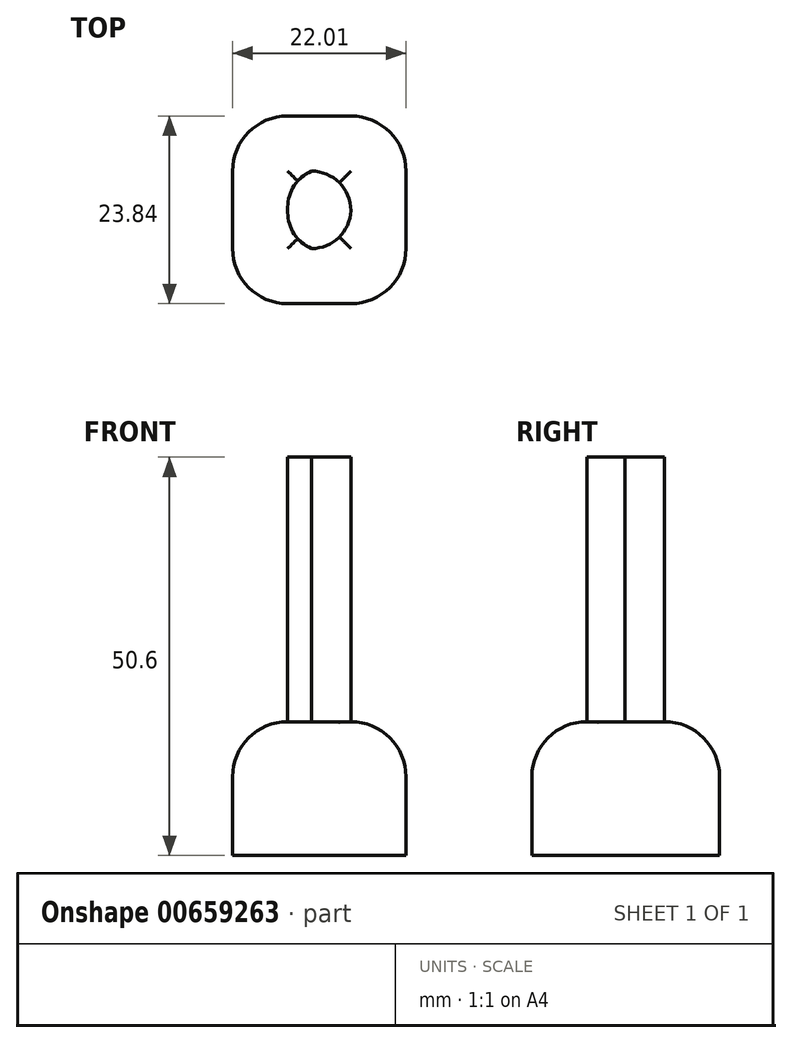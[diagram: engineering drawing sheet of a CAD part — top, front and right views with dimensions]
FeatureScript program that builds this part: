
annotation { "Feature Type Name" : "Feature", "Feature Type Description" : "" }
export const myFeature = defineFeature(function(context is Context, id is Id, definition is map)
    precondition{}
    {
        {
            var Q0;
            Q0=qCreatedBy(makeId("Top.planeOp"),FACE);
            var sketch = newSketch(context, id + "F0", { "sketchPlane" : qUnion([Q0])});
            skLineSegment(sketch, "E0.bottom", {"start": v(-41.92, -36.53) * mm, "end": v(-63.93, -36.53) * mm});
            skLineSegment(sketch, "E0.top", {"start": v(-41.92, -60.37) * mm, "end": v(-63.93, -60.37) * mm});
            skLineSegment(sketch, "E0.left", {"start": v(-41.92, -36.53) * mm, "end": v(-41.92, -60.37) * mm});
            skLineSegment(sketch, "E0.right", {"start": v(-63.93, -36.53) * mm, "end": v(-63.93, -60.37) * mm});
            skPoint(sketch, "E0.middle", {"position": v(-52.93, -48.45) * mm});
            skSolve(sketch);
        }
        {
            var Q0;
            Q0 = qSketchRegion(id + "F0", true);
            extrude(context, id + "F1", {"entities" : qUnion([Q0]), "depth" : 17 * mm, "offsetDistance" : 25 * mm});
        }
        {
            var Q0;
            Q0=makeQuery(id+"F1.opExtrude","CAP_EDGE",EDGE,{"disambiguationData":[OSD([sQuery(id+"F0.wireOp",EDGE,"E0.top")])],"isStart":false});
            fillet(context, id + "F2", {"entities" : qUnion([Q0]), "radius" : 7 * mm, "tangentPropagation" : true, "allowEdgeOverflow" : false});
        }
        {
            var Q0;
            Q0=makeQuery(id+"F1.opExtrude","CAP_EDGE",EDGE,{"disambiguationData":[OSD([sQuery(id+"F0.wireOp",EDGE,"E0.bottom")])],"isStart":false});
            var Q1;
            Q1=makeQuery(id+"F1.opExtrude","CAP_EDGE",EDGE,{"disambiguationData":[OSD([sQuery(id+"F0.wireOp",EDGE,"E0.left")])],"isStart":false});
            var Q2;
            Q2=makeQuery(id+"F1.opExtrude","CAP_EDGE",EDGE,{"disambiguationData":[OSD([sQuery(id+"F0.wireOp",EDGE,"E0.right")])],"isStart":false});
            fillet(context, id + "F3", {"entities" : qUnion([Q0, Q1, Q2]), "radius" : 7 * mm, "tangentPropagation" : true, "allowEdgeOverflow" : false});
        }
        {
            var Q0;
            Q0=makeQuery(id+"F1.opExtrude","SWEPT_EDGE",EDGE,{"disambiguationData":[OSD([sQuery(id+"F0.wireOp",EDGE,"E0.bottom"),sQuery(id+"F0.wireOp",EDGE,"E0.right")])]});
            fillet(context, id + "F4", {"entities" : qUnion([Q0]), "radius" : 7 * mm, "tangentPropagation" : true, "allowEdgeOverflow" : false});
        }
        {
            var Q0;
            Q0=makeQuery(id+"F1.opExtrude","SWEPT_EDGE",EDGE,{"disambiguationData":[OSD([sQuery(id+"F0.wireOp",EDGE,"E0.bottom"),sQuery(id+"F0.wireOp",EDGE,"E0.left")])]});
            fillet(context, id + "F5", {"entities" : qUnion([Q0]), "radius" : 7 * mm, "tangentPropagation" : true, "allowEdgeOverflow" : false});
        }
        {
            var Q0;
            Q0=makeQuery(id+"F1.opExtrude","CAP_FACE",FACE,{"disambiguationData":[OSD([sQuery(id+"F0.wireOp",EDGE,"E0.bottom"),sQuery(id+"F0.wireOp",EDGE,"E0.top"),sQuery(id+"F0.wireOp",EDGE,"E0.left"),sQuery(id+"F0.wireOp",EDGE,"E0.right")])],"isStart":false});
            extrude(context, id + "F6", {"entities" : qUnion([Q0]), "operationType" : NewBodyOperationType.ADD, "depth" : 33.6 * mm, "offsetDistance" : 25 * mm});
        }
        {
            var Q0;
            {var subQ0=sQuery(id+"F0.wireOp",EDGE,"E0.bottom");var subQ1=sQuery(id+"F0.wireOp",EDGE,"E0.right");var subQ2=sQuery(id+"F0.wireOp",EDGE,"E0.left");var subQ3=sQuery(id+"F0.wireOp",EDGE,"E0.top");Q0=makeQuery(id+"F6.opExtrude","SWEPT_EDGE",EDGE,{"disambiguationData":[OSD([subQ0,subQ3,subQ2,subQ1]),TDD([makeQuery(id+"F5.opFillet","BLEND_VERTEX",VERTEX,{"blendedFrom":[makeQuery(id+"F3.opFillet","BLEND_EDGE",EDGE,{"blendedFrom":[makeQuery(id+"F1.opExtrude","CAP_EDGE",EDGE,{"disambiguationData":[OSD([subQ0])],"isStart":false}),makeQuery(id+"F1.opExtrude","CAP_EDGE",EDGE,{"disambiguationData":[OSD([subQ2])],"isStart":false})],"blendedInto":[]}),makeQuery(id+"F3.opFillet","BLEND_FACE",FACE,{"disambiguationData":[OSD([subQ2])]}),makeQuery(id+"F1.opExtrude","CAP_FACE",FACE,{"disambiguationData":[OSD([subQ0,subQ3,subQ2,subQ1])],"isStart":false}),makeQuery(id+"F3.opFillet","BLEND_FACE",FACE,{"disambiguationData":[OSD([subQ0])]})],"blendedInto":[makeQuery(id+"F3.opFillet","BLEND_FACE",FACE,{"disambiguationData":[OSD([subQ2])]}),makeQuery(id+"F1.opExtrude","CAP_FACE",FACE,{"disambiguationData":[OSD([subQ0,subQ3,subQ2,subQ1])],"isStart":false}),makeQuery(id+"F3.opFillet","BLEND_FACE",FACE,{"disambiguationData":[OSD([subQ0])]})]})])]});}
            fillet(context, id + "F7", {"entities" : qUnion([Q0]), "radius" : 5 * mm, "tangentPropagation" : true, "allowEdgeOverflow" : false});
        }
        {
            var Q0;
            {var subQ0=sQuery(id+"F0.wireOp",EDGE,"E0.right");var subQ1=sQuery(id+"F0.wireOp",EDGE,"E0.left");var subQ2=sQuery(id+"F0.wireOp",EDGE,"E0.top");var subQ3=sQuery(id+"F0.wireOp",EDGE,"E0.bottom");Q0=makeQuery(id+"F6.opExtrude","SWEPT_EDGE",EDGE,{"disambiguationData":[OSD([subQ3,subQ2,subQ1,subQ0]),TDD([makeQuery(id+"F4.opFillet","BLEND_VERTEX",VERTEX,{"blendedFrom":[makeQuery(id+"F3.opFillet","BLEND_EDGE",EDGE,{"blendedFrom":[makeQuery(id+"F1.opExtrude","CAP_EDGE",EDGE,{"disambiguationData":[OSD([subQ3])],"isStart":false}),makeQuery(id+"F1.opExtrude","CAP_EDGE",EDGE,{"disambiguationData":[OSD([subQ0])],"isStart":false})],"blendedInto":[]}),makeQuery(id+"F3.opFillet","BLEND_FACE",FACE,{"disambiguationData":[OSD([subQ3])]}),makeQuery(id+"F3.opFillet","BLEND_FACE",FACE,{"disambiguationData":[OSD([subQ0])]}),makeQuery(id+"F1.opExtrude","CAP_FACE",FACE,{"disambiguationData":[OSD([subQ3,subQ2,subQ1,subQ0])],"isStart":false})],"blendedInto":[makeQuery(id+"F3.opFillet","BLEND_FACE",FACE,{"disambiguationData":[OSD([subQ3])]}),makeQuery(id+"F3.opFillet","BLEND_FACE",FACE,{"disambiguationData":[OSD([subQ0])]}),makeQuery(id+"F1.opExtrude","CAP_FACE",FACE,{"disambiguationData":[OSD([subQ3,subQ2,subQ1,subQ0])],"isStart":false})]})])]});}
            fillet(context, id + "F8", {"entities" : qUnion([Q0]), "radius" : 5 * mm, "tangentPropagation" : true, "allowEdgeOverflow" : false});
        }
        {
            var Q0;
            {var subQ0=sQuery(id+"F0.wireOp",EDGE,"E0.right");var subQ1=sQuery(id+"F0.wireOp",EDGE,"E0.left");var subQ2=sQuery(id+"F0.wireOp",EDGE,"E0.top");var subQ3=sQuery(id+"F0.wireOp",EDGE,"E0.bottom");Q0=makeQuery(id+"F6.opExtrude","SWEPT_EDGE",EDGE,{"disambiguationData":[OSD([subQ3,subQ2,subQ1,subQ0]),TDD([makeQuery(id+"F3.opFillet","BLEND_VERTEX",VERTEX,{"blendedFrom":[makeQuery(id+"F2.opFillet","BLEND_EDGE",EDGE,{"blendedFrom":[makeQuery(id+"F1.opExtrude","CAP_EDGE",EDGE,{"disambiguationData":[OSD([subQ2])],"isStart":false}),makeQuery(id+"F1.opExtrude","SWEPT_FACE",FACE,{"disambiguationData":[OSD([subQ1])]})],"blendedInto":[makeQuery(id+"F1.opExtrude","SWEPT_FACE",FACE,{"disambiguationData":[OSD([subQ1])]})]}),makeQuery(id+"F1.opExtrude","CAP_EDGE",EDGE,{"disambiguationData":[OSD([subQ1])],"isStart":false}),makeQuery(id+"F2.opFillet","BLEND_FACE",FACE,{"disambiguationData":[OSD([subQ2])]}),makeQuery(id+"F1.opExtrude","CAP_FACE",FACE,{"disambiguationData":[OSD([subQ3,subQ2,subQ1,subQ0])],"isStart":false})],"blendedInto":[makeQuery(id+"F2.opFillet","BLEND_FACE",FACE,{"disambiguationData":[OSD([subQ2])]}),makeQuery(id+"F1.opExtrude","CAP_FACE",FACE,{"disambiguationData":[OSD([subQ3,subQ2,subQ1,subQ0])],"isStart":false})]})])]});}
            fillet(context, id + "F9", {"entities" : qUnion([Q0]), "radius" : 5 * mm, "tangentPropagation" : true, "allowEdgeOverflow" : false});
        }
        {
            var Q0;
            {var subQ0=sQuery(id+"F0.wireOp",EDGE,"E0.right");var subQ1=sQuery(id+"F0.wireOp",EDGE,"E0.left");var subQ2=sQuery(id+"F0.wireOp",EDGE,"E0.top");var subQ3=sQuery(id+"F0.wireOp",EDGE,"E0.bottom");Q0=makeQuery(id+"F6.opExtrude","SWEPT_EDGE",EDGE,{"disambiguationData":[OSD([subQ3,subQ2,subQ1,subQ0]),TDD([makeQuery(id+"F3.opFillet","BLEND_VERTEX",VERTEX,{"blendedFrom":[makeQuery(id+"F2.opFillet","BLEND_EDGE",EDGE,{"blendedFrom":[makeQuery(id+"F1.opExtrude","CAP_EDGE",EDGE,{"disambiguationData":[OSD([subQ2])],"isStart":false}),makeQuery(id+"F1.opExtrude","SWEPT_FACE",FACE,{"disambiguationData":[OSD([subQ0])]})],"blendedInto":[makeQuery(id+"F1.opExtrude","SWEPT_FACE",FACE,{"disambiguationData":[OSD([subQ0])]})]}),makeQuery(id+"F1.opExtrude","CAP_EDGE",EDGE,{"disambiguationData":[OSD([subQ0])],"isStart":false}),makeQuery(id+"F2.opFillet","BLEND_FACE",FACE,{"disambiguationData":[OSD([subQ2])]}),makeQuery(id+"F1.opExtrude","CAP_FACE",FACE,{"disambiguationData":[OSD([subQ3,subQ2,subQ1,subQ0])],"isStart":false})],"blendedInto":[makeQuery(id+"F2.opFillet","BLEND_FACE",FACE,{"disambiguationData":[OSD([subQ2])]}),makeQuery(id+"F1.opExtrude","CAP_FACE",FACE,{"disambiguationData":[OSD([subQ3,subQ2,subQ1,subQ0])],"isStart":false})]})])]});}
            fillet(context, id + "F10", {"entities" : qUnion([Q0]), "radius" : 5 * mm, "tangentPropagation" : true, "allowEdgeOverflow" : false});
        }
    });
